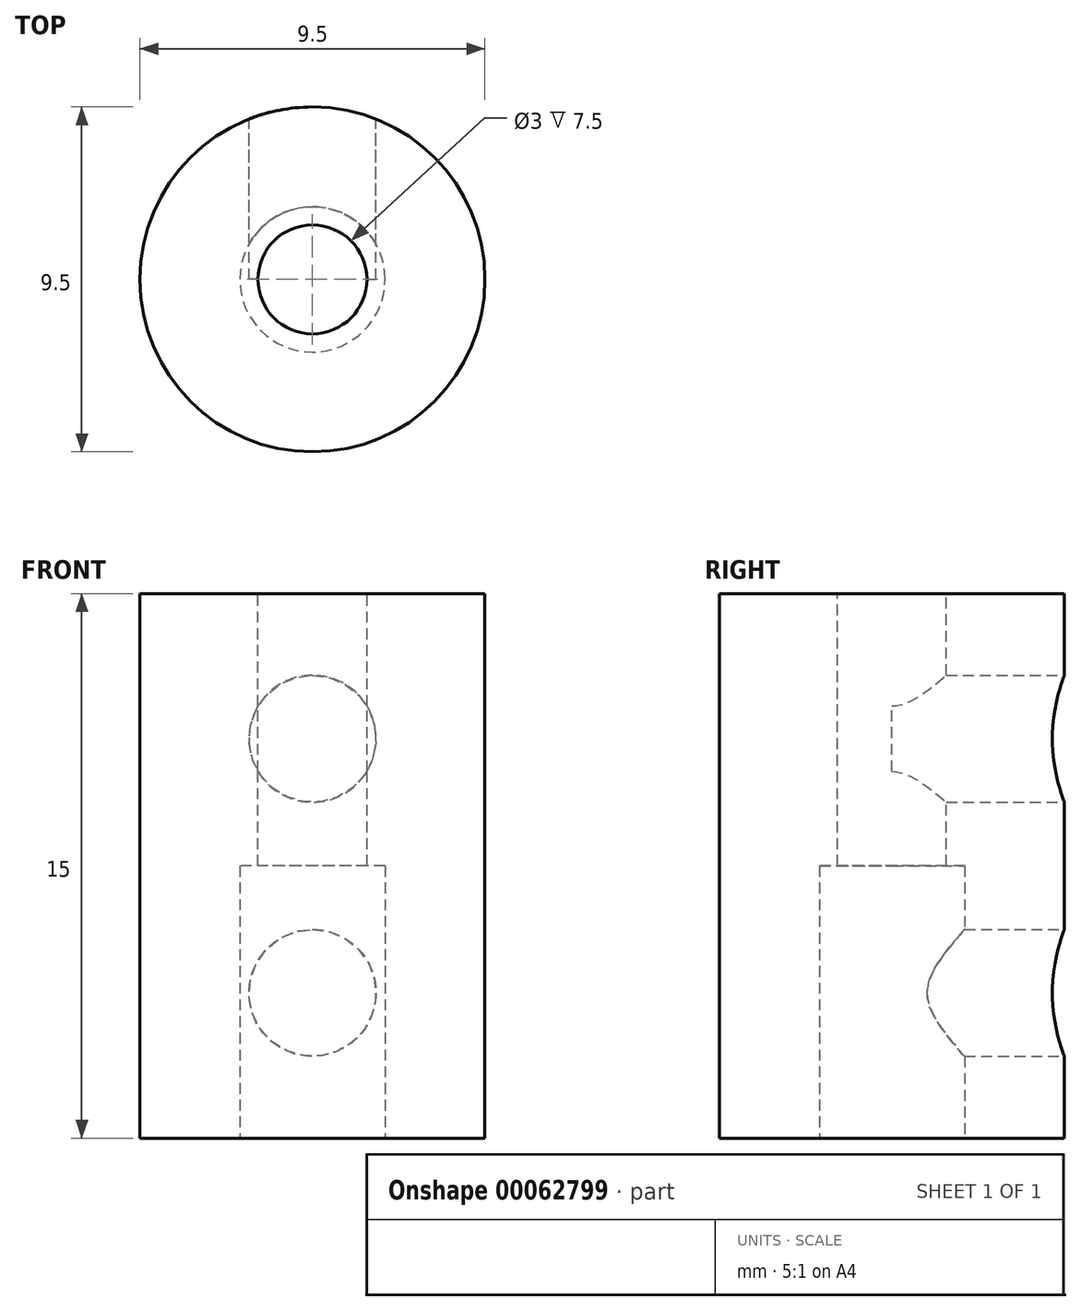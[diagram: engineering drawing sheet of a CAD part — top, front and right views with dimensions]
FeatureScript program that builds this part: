
annotation { "Feature Type Name" : "Feature", "Feature Type Description" : "" }
export const myFeature = defineFeature(function(context is Context, id is Id, definition is map)
    precondition{}
    {
        {
            var Q0;
            Q0=qCreatedBy(makeId("Top.planeOp"),FACE);
            var sketch = newSketch(context, id + "F0", { "sketchPlane" : qUnion([Q0])});
            skCircle(sketch, "E0", {"center": v(0, 0) * mm, "radius": 4.75 * mm});
            skSolve(sketch);
        }
        {
            var Q0;
            Q0=makeQuery(id+"F0.imprint","IMPRINT",FACE,{"disambiguationData":[TD([[makeQuery(id+"F0.imprint","IMPRINT",EDGE,{"derivedFrom":sQuery(id+"F0.wireOp",EDGE,"E0")}),1.0]])]});
            extrude(context, id + "F1", {"entities" : qUnion([Q0]), "depth" : 15 * mm});
        }
        {
            var Q0;
            Q0=makeQuery(id+"F1.opExtrude","CAP_FACE",FACE,{"disambiguationData":[OSD([sQuery(id+"F0.wireOp",EDGE,"E0")])],"isStart":false});
            var sketch = newSketch(context, id + "F2", { "sketchPlane" : qUnion([Q0])});
            skCircle(sketch, "E1", {"center": v(0, 0) * mm, "radius": 1.5 * mm});
            skSolve(sketch);
        }
        {
            var Q0;
            Q0=makeQuery(id+"F2.imprint","IMPRINT",FACE,{"disambiguationData":[TD([[makeQuery(id+"F2.imprint","IMPRINT",EDGE,{"derivedFrom":sQuery(id+"F2.wireOp",EDGE,"E1")}),1.0]])]});
            extrude(context, id + "F3", {"entities" : qUnion([Q0]), "operationType" : NewBodyOperationType.REMOVE, "oppositeDirection" : true, "depth" : 7.5 * mm});
        }
        {
            var Q0;
            Q0=qCreatedBy(makeId("Top.planeOp"),FACE);
            var sketch = newSketch(context, id + "F4", { "sketchPlane" : qUnion([Q0])});
            skCircle(sketch, "E2", {"center": v(0, 0) * mm, "radius": 2 * mm});
            skSolve(sketch);
        }
        {
            var Q0;
            Q0 = qSketchRegion(id + "F4", true);
            extrude(context, id + "F5", {"entities" : qUnion([Q0]), "operationType" : NewBodyOperationType.REMOVE, "depth" : 7.5 * mm});
        }
        {
            var Q0;
            Q0=qCreatedBy(makeId("Front.planeOp"),FACE);
            var sketch = newSketch(context, id + "F6", { "sketchPlane" : qUnion([Q0])});
            skLineSegment(sketch, "E3", {"start": v(0, 15) * mm, "end": v(0, 0) * mm, "construction": true});
            skPoint(sketch, "E4", {"position": v(0, 4) * mm});
            skSolve(sketch);
        }
        {
            var Q0;
            Q0=qCreatedBy(makeId("Front.planeOp"),FACE);
            var sketch = newSketch(context, id + "F7", { "sketchPlane" : qUnion([Q0])});
            skLineSegment(sketch, "E5", {"start": v(0, 15) * mm, "end": v(0, 0) * mm, "construction": true});
            skPoint(sketch, "E6", {"position": v(0, 11) * mm});
            skSolve(sketch);
        }
        {
            var Q0;
            Q0=sQuery(id+"F7.wireOp",VERTEX,"E6");
            var Q1;
            Q1=makeQuery(id+"F1.opExtrude","SWEPT_BODY",BODY,{"disambiguationData":[OSD([sQuery(id+"F0.wireOp",EDGE,"E0")])]});
            hole(context, id + "F8", {"style" : HoleStyle.SIMPLE, "holeDiameter" : 3.5 * mm, "endStyle" : HoleEndStyle.BLIND, "holeDepth" : 5 * mm, "locations" : qUnion([Q0]), "scope" : qUnion([Q1])});
        }
        {
            var Q0;
            Q0=sQuery(id+"F6.wireOp",VERTEX,"E4");
            var Q1;
            Q1=makeQuery(id+"F1.opExtrude","SWEPT_BODY",BODY,{"disambiguationData":[OSD([sQuery(id+"F0.wireOp",EDGE,"E0")])]});
            hole(context, id + "F9", {"style" : HoleStyle.SIMPLE, "holeDiameter" : 3.5 * mm, "endStyle" : HoleEndStyle.BLIND, "holeDepth" : 5 * mm, "locations" : qUnion([Q0]), "scope" : qUnion([Q1])});
        }
    });
